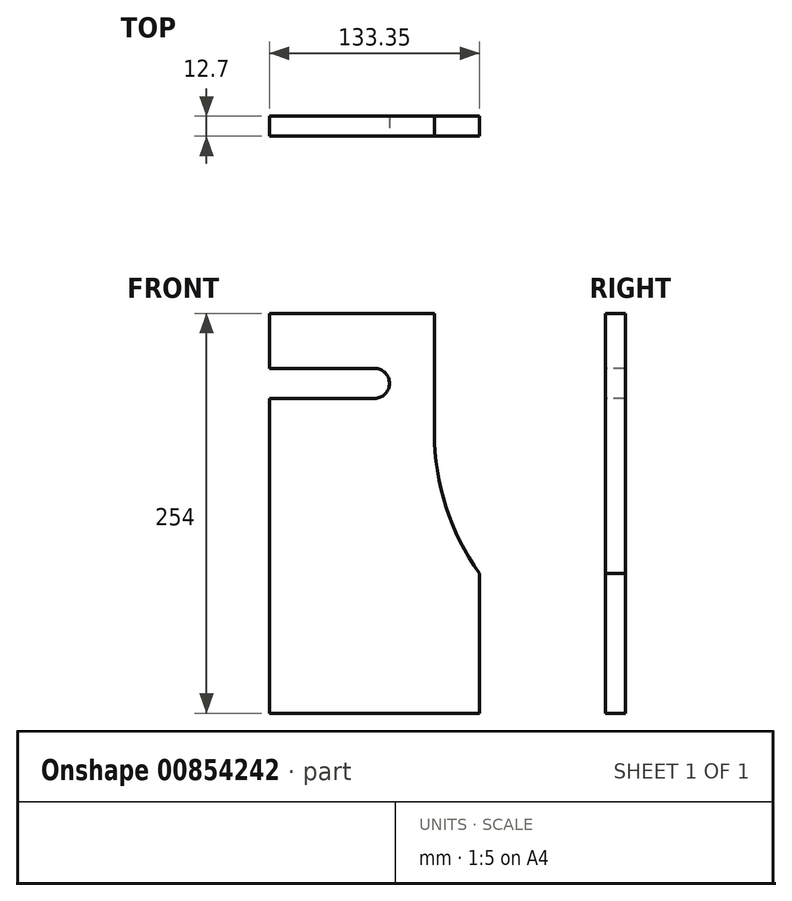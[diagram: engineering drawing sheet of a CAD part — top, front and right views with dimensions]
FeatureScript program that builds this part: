
annotation { "Feature Type Name" : "Feature", "Feature Type Description" : "" }
export const myFeature = defineFeature(function(context is Context, id is Id, definition is map)
    precondition{}
    {
        {
            var Q0;
            Q0=qCreatedBy(makeId("Front.planeOp"),FACE);
            var sketch = newSketch(context, id + "F0", { "sketchPlane" : qUnion([Q0])});
            skLineSegment(sketch, "E0", {"start": v(-66.67, -127) * mm, "end": v(-66.68, 127) * mm});
            skLineSegment(sketch, "E1", {"start": v(66.67, 127) * mm, "end": v(66.68, -127) * mm});
            skLineSegment(sketch, "E2", {"start": v(66.68, -127) * mm, "end": v(-66.67, -127) * mm});
            skLineSegment(sketch, "E3", {"start": v(-66.68, 127) * mm, "end": v(66.67, 127) * mm});
            skLineSegment(sketch, "E4", {"start": v(-66.68, 127) * mm, "end": v(66.68, -127) * mm, "construction": true});
            skSolve(sketch);
        }
        {
            var Q0;
            Q0=makeQuery(id+"F0.imprint","IMPRINT",FACE,{"disambiguationData":[TD([[makeQuery(id+"F0.imprint","IMPRINT",EDGE,{"derivedFrom":sQuery(id+"F0.wireOp",EDGE,"E0")}),-1.0]])]});
            extrude(context, id + "F1", {"entities" : qUnion([Q0]), "depth" : 12.7 * mm, "offsetDistance" : 25.4 * mm});
        }
        {
            var Q0;
            Q0=makeQuery(id+"F1.opExtrude","CAP_FACE",FACE,{"disambiguationData":[OSD([sQuery(id+"F0.wireOp",EDGE,"E0"),sQuery(id+"F0.wireOp",EDGE,"llpGFaMO-LiiQ-qMMw-QhUY-UvrnOBmCeLXD"),sQuery(id+"F0.wireOp",EDGE,"cxxX3X3e-vqej-k2xb-LDsN-ETGe2h5FuPCv"),sQuery(id+"F0.wireOp",EDGE,"E1"),sQuery(id+"F0.wireOp",EDGE,"E2")])],"isStart":false});
            var sketch = newSketch(context, id + "F2", { "sketchPlane" : qUnion([Q0])});
            skArc(sketch, "E5", {"start": v(0, 73.03) * mm, "mid": v(9.53, 82.55) * mm, "end": v(0, 92.08) * mm});
            skLineSegment(sketch, "E6", {"start": v(0, 92.08) * mm, "end": v(-66.67, 92.08) * mm});
            skLineSegment(sketch, "E7", {"start": v(0, 73.03) * mm, "end": v(-66.67, 73.03) * mm});
            skLineSegment(sketch, "E8", {"start": v(-66.67, 73.03) * mm, "end": v(-66.67, 92.08) * mm});
            skSolve(sketch);
        }
        {
            var Q0;
            Q0=qSketchRegion(id+"F0",true);
            var Q1;
            Q1=qSketchRegion(id+"F2",true);
            extrude(context, id + "F3", {"entities" : qUnion([Q0, Q1]), "operationType" : NewBodyOperationType.REMOVE, "endBound" : BoundingType.THROUGH_ALL, "oppositeDirection" : true, "depth" : 25.4 * mm, "offsetDistance" : 25.4 * mm});
        }
        {
            var Q0;
            Q0=makeQuery(id+"F1.opExtrude","CAP_FACE",FACE,{"disambiguationData":[OSD([sQuery(id+"F0.wireOp",EDGE,"E0"),sQuery(id+"F0.wireOp",EDGE,"E1"),sQuery(id+"F0.wireOp",EDGE,"E2"),sQuery(id+"F0.wireOp",EDGE,"E3")])],"isStart":false});
            var sketch = newSketch(context, id + "F4", { "sketchPlane" : qUnion([Q0])});
            skLineSegment(sketch, "E9", {"start": v(38.1, 127) * mm, "end": v(38.1, 50.8) * mm});
            skArc(sketch, "E10", {"start": v(38.1, 50.8) * mm, "mid": v(45.42, 4.11) * mm, "end": v(66.68, -38.1) * mm});
            skLineSegment(sketch, "E11.0", {"start": v(38.1, 127) * mm, "end": v(66.67, 127) * mm});
            skLineSegment(sketch, "E12.0", {"start": v(66.67, 127) * mm, "end": v(66.68, -38.1) * mm});
            skPoint(sketch, "E13.orphan", {"position": v(-66.68, 127) * mm});
            skPoint(sketch, "E14.orphan", {"position": v(66.68, -127) * mm});
            skSolve(sketch);
        }
        {
            var Q0;
            Q0=makeQuery(id+"F4.imprint","IMPRINT",FACE,{"disambiguationData":[TD([[makeQuery(id+"F4.imprint","IMPRINT",EDGE,{"derivedFrom":sQuery(id+"F4.wireOp",EDGE,"E9")}),1.0]])]});
            extrude(context, id + "F5", {"entities" : qUnion([Q0]), "operationType" : NewBodyOperationType.REMOVE, "endBound" : BoundingType.THROUGH_ALL, "oppositeDirection" : true, "depth" : 25.4 * mm, "offsetDistance" : 25.4 * mm});
        }
    });
